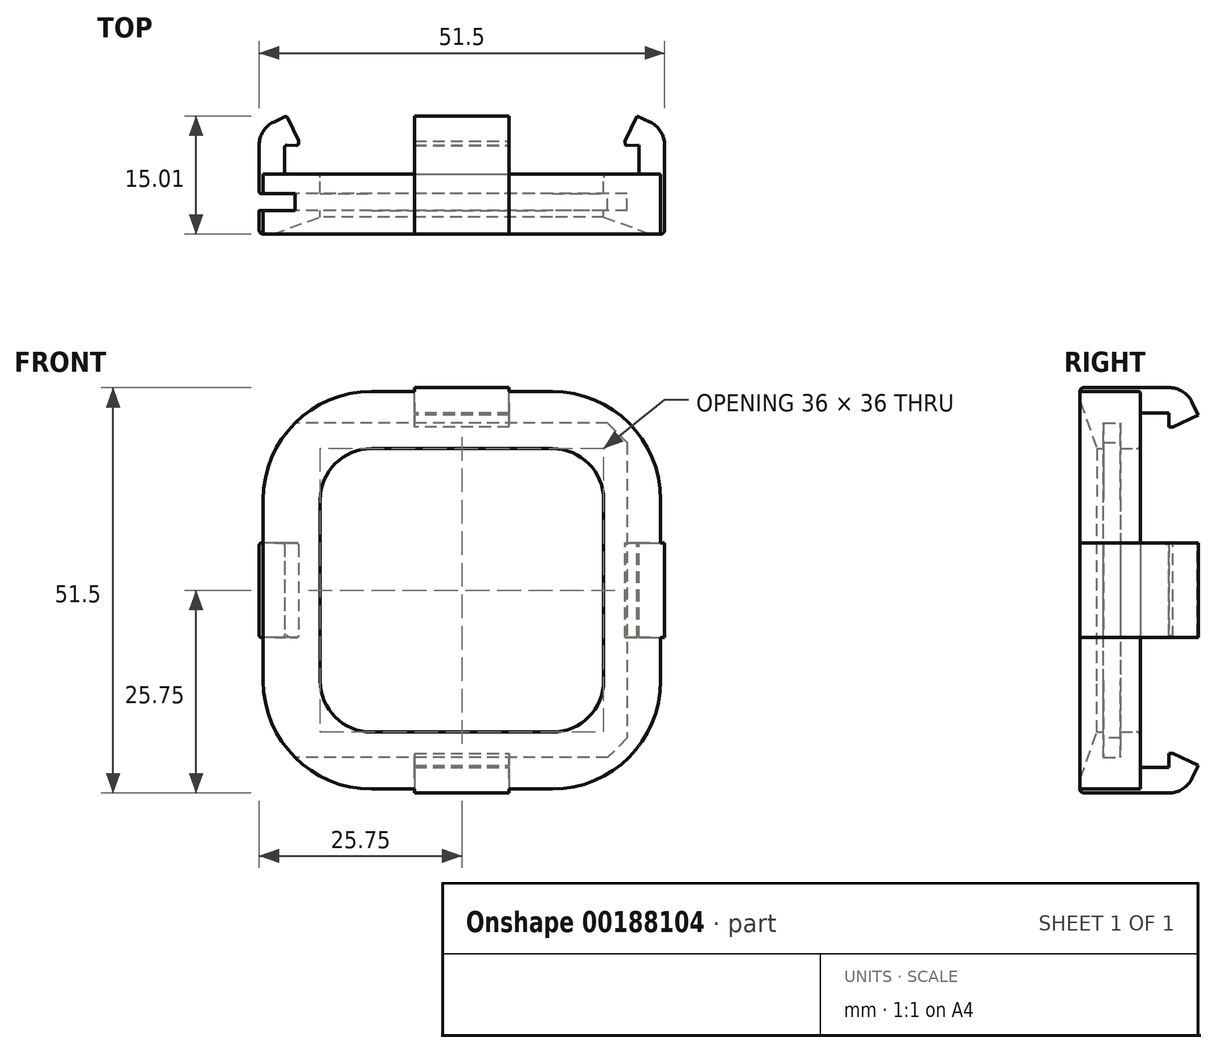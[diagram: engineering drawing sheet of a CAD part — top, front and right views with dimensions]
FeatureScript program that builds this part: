
annotation { "Feature Type Name" : "Feature", "Feature Type Description" : "" }
export const myFeature = defineFeature(function(context is Context, id is Id, definition is map)
    precondition{}
    {
        {
            var Q0;
            Q0=qCreatedBy(makeId("Front.planeOp"),FACE);
            var sketch = newSketch(context, id + "F0", { "sketchPlane" : qUnion([Q0])});
            skLineSegment(sketch, "E0.bottom", {"start": v(-11.5, 18) * mm, "end": v(11.5, 18) * mm});
            skLineSegment(sketch, "E0.top", {"start": v(-11.5, -18) * mm, "end": v(11.5, -18) * mm});
            skLineSegment(sketch, "E0.left", {"start": v(-18, 11.5) * mm, "end": v(-18, -11.5) * mm});
            skLineSegment(sketch, "E0.right", {"start": v(18, 11.5) * mm, "end": v(18, -11.5) * mm});
            skLineSegment(sketch, "E1", {"start": v(-11.5, 25.25) * mm, "end": v(11.5, 25.25) * mm});
            skLineSegment(sketch, "E2", {"start": v(25.25, 11.5) * mm, "end": v(25.25, -11.5) * mm});
            skLineSegment(sketch, "E3", {"start": v(11.5, -25.25) * mm, "end": v(-11.5, -25.25) * mm});
            skLineSegment(sketch, "E4", {"start": v(-25.25, -11.5) * mm, "end": v(-25.25, 11.5) * mm});
            skPoint(sketch, "E5.visualSharp", {"position": v(18, 18) * mm});
            skArc(sketch, "E5.filletArc", {"start": v(18, 11.5) * mm, "mid": v(16.1, 16.1) * mm, "end": v(11.5, 18) * mm});
            skPoint(sketch, "E6.visualSharp", {"position": v(-18, 18) * mm});
            skArc(sketch, "E6.filletArc", {"start": v(-11.5, 18) * mm, "mid": v(-16.1, 16.1) * mm, "end": v(-18, 11.5) * mm});
            skPoint(sketch, "E7.visualSharp", {"position": v(-18, -18) * mm});
            skArc(sketch, "E7.filletArc", {"start": v(-18, -11.5) * mm, "mid": v(-16.1, -16.1) * mm, "end": v(-11.5, -18) * mm});
            skPoint(sketch, "E8.visualSharp", {"position": v(18, -18) * mm});
            skArc(sketch, "E8.filletArc", {"start": v(11.5, -18) * mm, "mid": v(16.1, -16.1) * mm, "end": v(18, -11.5) * mm});
            skArc(sketch, "E9", {"start": v(-11.5, 25.25) * mm, "mid": v(-21.22, 21.22) * mm, "end": v(-25.25, 11.5) * mm});
            skArc(sketch, "E10", {"start": v(-25.25, -11.5) * mm, "mid": v(-21.22, -21.22) * mm, "end": v(-11.5, -25.25) * mm});
            skArc(sketch, "E11", {"start": v(11.5, -25.25) * mm, "mid": v(21.22, -21.22) * mm, "end": v(25.25, -11.5) * mm});
            skArc(sketch, "E12", {"start": v(25.25, 11.5) * mm, "mid": v(21.22, 21.22) * mm, "end": v(11.5, 25.25) * mm});
            skPoint(sketch, "E13.orphan", {"position": v(-25.25, 25.25) * mm});
            skPoint(sketch, "E14.orphan", {"position": v(-25.25, -25.25) * mm});
            skPoint(sketch, "E15.orphan", {"position": v(25.25, 25.25) * mm});
            skSolve(sketch);
        }
        {
            var Q0;
            Q0=makeQuery(id+"F0.imprint","IMPRINT",FACE,{"disambiguationData":[TD([[makeQuery(id+"F0.imprint","IMPRINT",EDGE,{"derivedFrom":sQuery(id+"F0.wireOp",EDGE,"E0.bottom")}),1.0]])]});
            extrude(context, id + "F1", {"entities" : qUnion([Q0]), "depth" : 7.65 * mm});
        }
        {
            var Q0;
            Q0=qCreatedBy(makeId("Right.planeOp"),FACE);
            var sketch = newSketch(context, id + "F2", { "sketchPlane" : qUnion([Q0])});
            skLineSegment(sketch, "E16", {"start": v(-2.5, 21.25) * mm, "end": v(-2.5, -21.25) * mm});
            skLineSegment(sketch, "E17", {"start": v(-2.5, -21.25) * mm, "end": v(-4.65, -21.25) * mm});
            skLineSegment(sketch, "E18", {"start": v(-4.65, -21.25) * mm, "end": v(-4.65, 21.25) * mm});
            skLineSegment(sketch, "E19", {"start": v(-4.65, 21.25) * mm, "end": v(-2.5, 21.25) * mm});
            skSolve(sketch);
        }
        {
            var Q0;
            Q0=makeQuery(id+"F2.imprint","IMPRINT",FACE,{"disambiguationData":[TD([[makeQuery(id+"F2.imprint","IMPRINT",EDGE,{"derivedFrom":sQuery(id+"F2.wireOp",EDGE,"E16")}),-1.0]])]});
            extrude(context, id + "F3", {"entities" : qUnion([Q0]), "operationType" : NewBodyOperationType.REMOVE, "depth" : 21 * mm, "hasSecondDirection" : true, "secondDirectionBound" : SecondDirectionBoundingType.THROUGH_ALL, "secondDirectionOppositeDirection" : true, "secondDirectionDepth" : 25 * mm});
        }
        {
            var Q0;
            Q0=makeQuery(id+"F3.boolean.opBoolean","COPY",EDGE,{"derivedFrom":makeQuery(id+"F3.opExtrude","CAP_EDGE",EDGE,{"disambiguationData":[OSD([sQuery(id+"F2.wireOp",EDGE,"E19")])],"isStart":false})});
            var Q1;
            Q1=makeQuery(id+"F3.boolean.opBoolean","COPY",EDGE,{"derivedFrom":makeQuery(id+"F3.opExtrude","CAP_EDGE",EDGE,{"disambiguationData":[OSD([sQuery(id+"F2.wireOp",EDGE,"E17")])],"isStart":false})});
            chamfer(context, id + "F4", {"entities" : qUnion([Q0, Q1]), "width" : 2.5 * mm, "tangentPropagation" : true});
        }
        {
            var Q0;
            Q0=makeQuery(id+"F1.opExtrude","CAP_EDGE",EDGE,{"disambiguationData":[OSD([sQuery(id+"F0.wireOp",EDGE,"E0.top")])],"isStart":false});
            chamfer(context, id + "F5", {"entities" : qUnion([Q0]), "chamferType" : ChamferType.TWO_OFFSETS, "width1" : 2.15 * mm, "oppositeDirection" : false, "width2" : 6 * mm, "tangentPropagation" : true});
        }
        {
            var Q0;
            Q0=qCreatedBy(makeId("Right.planeOp"),FACE);
            var sketch = newSketch(context, id + "F6", { "sketchPlane" : qUnion([Q0])});
            skLineSegment(sketch, "E20", {"start": v(0, 25.25) * mm, "end": v(-7.65, 25.25) * mm});
            skLineSegment(sketch, "E21", {"start": v(-7.15, 25.75) * mm, "end": v(3.65, 25.75) * mm});
            skLineSegment(sketch, "E22", {"start": v(0, 22.5) * mm, "end": v(3.65, 22.5) * mm});
            skArc(sketch, "E23", {"start": v(-7.65, 25.25) * mm, "mid": v(-7.5, 25.6) * mm, "end": v(-7.15, 25.75) * mm});
            skArc(sketch, "E24", {"start": v(3.65, 25.75) * mm, "mid": v(5.4, 25.24) * mm, "end": v(6.6, 23.88) * mm});
            skLineSegment(sketch, "E25", {"start": v(3.65, 22.5) * mm, "end": v(3.62, 20.75) * mm});
            skLineSegment(sketch, "E26", {"start": v(6.6, 23.88) * mm, "end": v(7.36, 22.25) * mm});
            skLineSegment(sketch, "E27", {"start": v(0, 22.5) * mm, "end": v(0, 25.25) * mm});
            skLineSegment(sketch, "E28", {"start": v(4.15, 20.74) * mm, "end": v(7.36, 22.25) * mm});
            skLineSegment(sketch, "E29", {"start": v(3.62, 20.75) * mm, "end": v(4.15, 20.74) * mm});
            skSolve(sketch);
        }
        {
            var Q0;
            Q0=makeQuery(id+"F6.imprint","IMPRINT",FACE,{"disambiguationData":[TD([[makeQuery(id+"F6.imprint","IMPRINT",EDGE,{"derivedFrom":sQuery(id+"F6.wireOp",EDGE,"E20")}),-1.0]])]});
            extrude(context, id + "F7", {"entities" : qUnion([Q0]), "endBound" : BoundingType.SYMMETRIC, "depth" : 12 * mm});
        }
        {
            var Q0;
            Q0=qCreatedBy(makeId("Right.planeOp"),FACE);
            var sketch = newSketch(context, id + "F8", { "sketchPlane" : qUnion([Q0])});
            skLineSegment(sketch, "E30", {"start": v(44.47, 0) * mm, "end": v(-52.9, 0) * mm, "construction": true});
            skSolve(sketch);
        }
        {
            var Q0;
            Q0=makeQuery(id+"F7.opExtrude","SWEPT_BODY",BODY,{"disambiguationData":[OSD([sQuery(id+"F6.wireOp",EDGE,"E20"),sQuery(id+"F6.wireOp",EDGE,"E21"),sQuery(id+"F6.wireOp",EDGE,"E22"),sQuery(id+"F6.wireOp",EDGE,"E23"),sQuery(id+"F6.wireOp",EDGE,"E24"),sQuery(id+"F6.wireOp",EDGE,"E25"),sQuery(id+"F6.wireOp",EDGE,"E26"),sQuery(id+"F6.wireOp",EDGE,"jlcA28JM-81w5-koXz-N9Zr-FnXAcRdSVXKj"),sQuery(id+"F6.wireOp",EDGE,"E27")])]});
            var Q1;
            Q1=sQuery(id+"F8.wireOp",EDGE,"E30");
            circularPattern(context, id + "F9", {"entities" : qUnion([Q0]), "axis" : qUnion([Q1]), "angle" : 90 * degree, "instanceCount" : 4, "oppositeDirection" : true});
        }
        {
            var Q0;
            Q0 = qSketchRegion(id + "F2", true);
            extrude(context, id + "F10", {"entities" : qUnion([Q0]), "operationType" : NewBodyOperationType.REMOVE, "endBound" : BoundingType.THROUGH_ALL, "oppositeDirection" : true, "depth" : 25 * mm});
        }
        {
            var Q0;
            Q0=makeQuery(id+"F9.opPattern","COPY",BODY,{"derivedFrom":makeQuery(id+"F7.opExtrude","SWEPT_BODY",BODY,{"disambiguationData":[OSD([sQuery(id+"F6.wireOp",EDGE,"E20"),sQuery(id+"F6.wireOp",EDGE,"E21"),sQuery(id+"F6.wireOp",EDGE,"E22"),sQuery(id+"F6.wireOp",EDGE,"E23"),sQuery(id+"F6.wireOp",EDGE,"E24"),sQuery(id+"F6.wireOp",EDGE,"E25"),sQuery(id+"F6.wireOp",EDGE,"E26"),sQuery(id+"F6.wireOp",EDGE,"E27"),sQuery(id+"F6.wireOp",EDGE,"E28"),sQuery(id+"F6.wireOp",EDGE,"E29")])]}),"instanceName":"2"});
            var Q1;
            Q1=makeQuery(id+"F9.opPattern","COPY",BODY,{"derivedFrom":makeQuery(id+"F7.opExtrude","SWEPT_BODY",BODY,{"disambiguationData":[OSD([sQuery(id+"F6.wireOp",EDGE,"E20"),sQuery(id+"F6.wireOp",EDGE,"E21"),sQuery(id+"F6.wireOp",EDGE,"E22"),sQuery(id+"F6.wireOp",EDGE,"E23"),sQuery(id+"F6.wireOp",EDGE,"E24"),sQuery(id+"F6.wireOp",EDGE,"E25"),sQuery(id+"F6.wireOp",EDGE,"E26"),sQuery(id+"F6.wireOp",EDGE,"E27"),sQuery(id+"F6.wireOp",EDGE,"E28"),sQuery(id+"F6.wireOp",EDGE,"E29")])]}),"instanceName":"1"});
            var Q2;
            Q2=makeQuery(id+"F1.opExtrude","SWEPT_BODY",BODY,{"disambiguationData":[OSD([sQuery(id+"F0.wireOp",EDGE,"E0.bottom"),sQuery(id+"F0.wireOp",EDGE,"E0.top"),sQuery(id+"F0.wireOp",EDGE,"E0.left"),sQuery(id+"F0.wireOp",EDGE,"E0.right"),sQuery(id+"F0.wireOp",EDGE,"E1"),sQuery(id+"F0.wireOp",EDGE,"E2"),sQuery(id+"F0.wireOp",EDGE,"E3"),sQuery(id+"F0.wireOp",EDGE,"E4"),sQuery(id+"F0.wireOp",EDGE,"E5.filletArc"),sQuery(id+"F0.wireOp",EDGE,"E6.filletArc"),sQuery(id+"F0.wireOp",EDGE,"E7.filletArc"),sQuery(id+"F0.wireOp",EDGE,"E8.filletArc"),sQuery(id+"F0.wireOp",EDGE,"E9"),sQuery(id+"F0.wireOp",EDGE,"E10"),sQuery(id+"F0.wireOp",EDGE,"E11"),sQuery(id+"F0.wireOp",EDGE,"E12")])]});
            var Q3;
            Q3=makeQuery(id+"F7.opExtrude","SWEPT_BODY",BODY,{"disambiguationData":[OSD([sQuery(id+"F6.wireOp",EDGE,"E20"),sQuery(id+"F6.wireOp",EDGE,"E21"),sQuery(id+"F6.wireOp",EDGE,"E22"),sQuery(id+"F6.wireOp",EDGE,"E23"),sQuery(id+"F6.wireOp",EDGE,"E24"),sQuery(id+"F6.wireOp",EDGE,"E25"),sQuery(id+"F6.wireOp",EDGE,"E26"),sQuery(id+"F6.wireOp",EDGE,"E27"),sQuery(id+"F6.wireOp",EDGE,"E28"),sQuery(id+"F6.wireOp",EDGE,"E29")])]});
            booleanBodies(context, id + "F11", {"operationType" : BooleanOperationType.UNION, "tools" : qUnion([Q0, Q1, Q2, Q3])});
        }
        {
            var Q0;
            Q0=makeQuery(id+"F7.opExtrude","CAP_EDGE",EDGE,{"disambiguationData":[OSD([sQuery(id+"F6.wireOp",EDGE,"E20")])],"isStart":true});
            var Q1;
            Q1=makeQuery(id+"F7.opExtrude","CAP_EDGE",EDGE,{"disambiguationData":[OSD([sQuery(id+"F6.wireOp",EDGE,"E27")])],"isStart":true});
            var Q2;
            {var subQ1=sQuery(id+"F0.wireOp",EDGE,"E9");var subQ2=sQuery(id+"F0.wireOp",EDGE,"E1");Q2=makeQuery(id+"F11.opBoolean","SPLIT",EDGE,{"disambiguationData":[TD([makeQuery(id+"F1.opExtrude","SWEPT_FACE",FACE,{"disambiguationData":[OSD([subQ1])]})])],"derivedFrom":makeQuery(id+"F1.opExtrude","CAP_EDGE",EDGE,{"disambiguationData":[OSD([subQ2])],"isStart":false})});}
            var Q3;
            Q3=makeQuery(id+"F7.opExtrude","CAP_EDGE",EDGE,{"disambiguationData":[OSD([sQuery(id+"F6.wireOp",EDGE,"E21")])],"isStart":true});
            var Q4;
            Q4=makeQuery(id+"F7.opExtrude","SWEPT_EDGE",EDGE,{"disambiguationData":[OSD([sQuery(id+"F6.wireOp",EDGE,"E26"),sQuery(id+"F6.wireOp",EDGE,"E28")])]});
            var Q5;
            Q5=makeQuery(id+"F7.opExtrude","CAP_EDGE",EDGE,{"disambiguationData":[OSD([sQuery(id+"F6.wireOp",EDGE,"E26")])],"isStart":false});
            var Q6;
            Q6=makeQuery(id+"F7.opExtrude","CAP_EDGE",EDGE,{"disambiguationData":[OSD([sQuery(id+"F6.wireOp",EDGE,"E20")])],"isStart":false});
            var Q7;
            Q7=makeQuery(id+"F7.opExtrude","CAP_EDGE",EDGE,{"disambiguationData":[OSD([sQuery(id+"F6.wireOp",EDGE,"E21")])],"isStart":false});
            var Q8;
            Q8=makeQuery(id+"F7.opExtrude","CAP_EDGE",EDGE,{"disambiguationData":[OSD([sQuery(id+"F6.wireOp",EDGE,"E24")])],"isStart":false});
            var Q9;
            Q9=makeQuery(id+"F7.opExtrude","CAP_EDGE",EDGE,{"disambiguationData":[OSD([sQuery(id+"F6.wireOp",EDGE,"E23")])],"isStart":false});
            var Q10;
            {var subQ1=sQuery(id+"F0.wireOp",EDGE,"E1");var subQ2=sQuery(id+"F0.wireOp",EDGE,"E12");Q10=makeQuery(id+"F11.opBoolean","SPLIT",EDGE,{"disambiguationData":[TD([makeQuery(id+"F1.opExtrude","SWEPT_FACE",FACE,{"disambiguationData":[OSD([subQ2])]})])],"derivedFrom":makeQuery(id+"F1.opExtrude","CAP_EDGE",EDGE,{"disambiguationData":[OSD([subQ1])],"isStart":false})});}
            var Q11;
            Q11=makeQuery(id+"F7.opExtrude","CAP_EDGE",EDGE,{"disambiguationData":[OSD([sQuery(id+"F6.wireOp",EDGE,"E27")])],"isStart":false});
            var Q12;
            Q12=makeQuery(id+"F7.opExtrude","SWEPT_EDGE",EDGE,{"disambiguationData":[OSD([sQuery(id+"F6.wireOp",EDGE,"E22"),sQuery(id+"F6.wireOp",EDGE,"E25")])]});
            var Q13;
            Q13=makeQuery(id+"F7.opExtrude","CAP_EDGE",EDGE,{"disambiguationData":[OSD([sQuery(id+"F6.wireOp",EDGE,"E25")])],"isStart":true});
            var Q14;
            Q14=makeQuery(id+"F7.opExtrude","CAP_EDGE",EDGE,{"disambiguationData":[OSD([sQuery(id+"F6.wireOp",EDGE,"E29")])],"isStart":true});
            var Q15;
            Q15=makeQuery(id+"F7.opExtrude","CAP_EDGE",EDGE,{"disambiguationData":[OSD([sQuery(id+"F6.wireOp",EDGE,"E28")])],"isStart":true});
            var Q16;
            Q16=makeQuery(id+"F7.opExtrude","SWEPT_EDGE",EDGE,{"disambiguationData":[OSD([sQuery(id+"F6.wireOp",EDGE,"E25"),sQuery(id+"F6.wireOp",EDGE,"E29")])]});
            var Q17;
            Q17=makeQuery(id+"F7.opExtrude","SWEPT_EDGE",EDGE,{"disambiguationData":[OSD([sQuery(id+"F6.wireOp",EDGE,"E28"),sQuery(id+"F6.wireOp",EDGE,"E29")])]});
            var Q18;
            Q18=makeQuery(id+"F7.opExtrude","CAP_EDGE",EDGE,{"disambiguationData":[OSD([sQuery(id+"F6.wireOp",EDGE,"E22")])],"isStart":false});
            var Q19;
            Q19=makeQuery(id+"F7.opExtrude","CAP_EDGE",EDGE,{"disambiguationData":[OSD([sQuery(id+"F6.wireOp",EDGE,"E28")])],"isStart":false});
            var Q20;
            Q20=makeQuery(id+"F7.opExtrude","CAP_EDGE",EDGE,{"disambiguationData":[OSD([sQuery(id+"F6.wireOp",EDGE,"E29")])],"isStart":false});
            var Q21;
            Q21=makeQuery(id+"F3.boolean.opBoolean","INTERSECT",EDGE,{"derivedFrom":[makeQuery(id+"F1.opExtrude","SWEPT_FACE",FACE,{"disambiguationData":[OSD([sQuery(id+"F0.wireOp",EDGE,"E4")])]}),makeQuery(id+"F3.opExtrude","SWEPT_FACE",FACE,{"disambiguationData":[OSD([sQuery(id+"F2.wireOp",EDGE,"E16")])]})]});
            var Q22;
            Q22=makeQuery(id+"F10.boolean.opBoolean","INTERSECT",EDGE,{"derivedFrom":[makeQuery(id+"F9.opPattern","COPY",FACE,{"derivedFrom":makeQuery(id+"F7.opExtrude","CAP_FACE",FACE,{"disambiguationData":[OSD([sQuery(id+"F6.wireOp",EDGE,"E20"),sQuery(id+"F6.wireOp",EDGE,"E21"),sQuery(id+"F6.wireOp",EDGE,"E22"),sQuery(id+"F6.wireOp",EDGE,"E23"),sQuery(id+"F6.wireOp",EDGE,"E24"),sQuery(id+"F6.wireOp",EDGE,"E25"),sQuery(id+"F6.wireOp",EDGE,"E26"),sQuery(id+"F6.wireOp",EDGE,"E27"),sQuery(id+"F6.wireOp",EDGE,"E28"),sQuery(id+"F6.wireOp",EDGE,"E29")])],"isStart":true}),"instanceName":"3"}),makeQuery(id+"F10.opExtrude","SWEPT_FACE",FACE,{"disambiguationData":[OSD([sQuery(id+"F2.wireOp",EDGE,"E16")])]})]});
            var Q23;
            {var subQ0=sQuery(id+"F0.wireOp",EDGE,"E9");var subQ1=sQuery(id+"F0.wireOp",EDGE,"E1");Q23=makeQuery(id+"F11.opBoolean","SPLIT",EDGE,{"disambiguationData":[TD([makeQuery(id+"F1.opExtrude","SWEPT_FACE",FACE,{"disambiguationData":[OSD([subQ0])]})])],"derivedFrom":makeQuery(id+"F1.opExtrude","CAP_EDGE",EDGE,{"disambiguationData":[OSD([subQ1])],"isStart":true})});}
            var Q24;
            Q24=makeQuery(id+"F9.opPattern","COPY",EDGE,{"derivedFrom":makeQuery(id+"F7.opExtrude","CAP_EDGE",EDGE,{"disambiguationData":[OSD([sQuery(id+"F6.wireOp",EDGE,"E20")])],"isStart":false}),"instanceName":"2"});
            var Q25;
            Q25=makeQuery(id+"F9.opPattern","COPY",EDGE,{"derivedFrom":makeQuery(id+"F7.opExtrude","CAP_EDGE",EDGE,{"disambiguationData":[OSD([sQuery(id+"F6.wireOp",EDGE,"E27")])],"isStart":false}),"instanceName":"2"});
            var Q26;
            Q26=makeQuery(id+"F9.opPattern","COPY",EDGE,{"derivedFrom":makeQuery(id+"F7.opExtrude","CAP_EDGE",EDGE,{"disambiguationData":[OSD([sQuery(id+"F6.wireOp",EDGE,"E23")])],"isStart":false}),"instanceName":"2"});
            var Q27;
            {var subQ1=sQuery(id+"F0.wireOp",EDGE,"E3");var subQ2=sQuery(id+"F0.wireOp",EDGE,"E10");Q27=makeQuery(id+"F11.opBoolean","SPLIT",EDGE,{"disambiguationData":[TD([makeQuery(id+"F1.opExtrude","SWEPT_FACE",FACE,{"disambiguationData":[OSD([subQ2])]})])],"derivedFrom":makeQuery(id+"F1.opExtrude","CAP_EDGE",EDGE,{"disambiguationData":[OSD([subQ1])],"isStart":false})});}
            var Q28;
            Q28=makeQuery(id+"F9.opPattern","COPY",EDGE,{"derivedFrom":makeQuery(id+"F7.opExtrude","CAP_EDGE",EDGE,{"disambiguationData":[OSD([sQuery(id+"F6.wireOp",EDGE,"E22")])],"isStart":false}),"instanceName":"2"});
            var Q29;
            Q29=makeQuery(id+"F9.opPattern","COPY",EDGE,{"derivedFrom":makeQuery(id+"F7.opExtrude","CAP_EDGE",EDGE,{"disambiguationData":[OSD([sQuery(id+"F6.wireOp",EDGE,"E25")])],"isStart":false}),"instanceName":"2"});
            var Q30;
            Q30=makeQuery(id+"F9.opPattern","COPY",EDGE,{"derivedFrom":makeQuery(id+"F7.opExtrude","CAP_EDGE",EDGE,{"disambiguationData":[OSD([sQuery(id+"F6.wireOp",EDGE,"E29")])],"isStart":false}),"instanceName":"2"});
            var Q31;
            Q31=makeQuery(id+"F9.opPattern","COPY",EDGE,{"derivedFrom":makeQuery(id+"F7.opExtrude","CAP_EDGE",EDGE,{"disambiguationData":[OSD([sQuery(id+"F6.wireOp",EDGE,"E28")])],"isStart":false}),"instanceName":"2"});
            var Q32;
            Q32=makeQuery(id+"F9.opPattern","COPY",EDGE,{"derivedFrom":makeQuery(id+"F7.opExtrude","SWEPT_EDGE",EDGE,{"disambiguationData":[OSD([sQuery(id+"F6.wireOp",EDGE,"E26"),sQuery(id+"F6.wireOp",EDGE,"E28")])]}),"instanceName":"2"});
            var Q33;
            Q33=makeQuery(id+"F9.opPattern","COPY",EDGE,{"derivedFrom":makeQuery(id+"F7.opExtrude","SWEPT_EDGE",EDGE,{"disambiguationData":[OSD([sQuery(id+"F6.wireOp",EDGE,"E28"),sQuery(id+"F6.wireOp",EDGE,"E29")])]}),"instanceName":"2"});
            var Q34;
            Q34=makeQuery(id+"F9.opPattern","COPY",EDGE,{"derivedFrom":makeQuery(id+"F7.opExtrude","SWEPT_EDGE",EDGE,{"disambiguationData":[OSD([sQuery(id+"F6.wireOp",EDGE,"E22"),sQuery(id+"F6.wireOp",EDGE,"E25")])]}),"instanceName":"2"});
            var Q35;
            Q35=makeQuery(id+"F9.opPattern","COPY",EDGE,{"derivedFrom":makeQuery(id+"F7.opExtrude","SWEPT_EDGE",EDGE,{"disambiguationData":[OSD([sQuery(id+"F6.wireOp",EDGE,"E25"),sQuery(id+"F6.wireOp",EDGE,"E29")])]}),"instanceName":"2"});
            var Q36;
            Q36=makeQuery(id+"F9.opPattern","COPY",EDGE,{"derivedFrom":makeQuery(id+"F7.opExtrude","CAP_EDGE",EDGE,{"disambiguationData":[OSD([sQuery(id+"F6.wireOp",EDGE,"E27")])],"isStart":true}),"instanceName":"2"});
            var Q37;
            Q37=makeQuery(id+"F9.opPattern","COPY",EDGE,{"derivedFrom":makeQuery(id+"F7.opExtrude","CAP_EDGE",EDGE,{"disambiguationData":[OSD([sQuery(id+"F6.wireOp",EDGE,"E22")])],"isStart":true}),"instanceName":"2"});
            var Q38;
            Q38=makeQuery(id+"F9.opPattern","COPY",EDGE,{"derivedFrom":makeQuery(id+"F7.opExtrude","CAP_EDGE",EDGE,{"disambiguationData":[OSD([sQuery(id+"F6.wireOp",EDGE,"E29")])],"isStart":true}),"instanceName":"2"});
            var Q39;
            Q39=makeQuery(id+"F9.opPattern","COPY",EDGE,{"derivedFrom":makeQuery(id+"F7.opExtrude","CAP_EDGE",EDGE,{"disambiguationData":[OSD([sQuery(id+"F6.wireOp",EDGE,"E28")])],"isStart":true}),"instanceName":"2"});
            var Q40;
            Q40=makeQuery(id+"F9.opPattern","COPY",EDGE,{"derivedFrom":makeQuery(id+"F7.opExtrude","CAP_EDGE",EDGE,{"disambiguationData":[OSD([sQuery(id+"F6.wireOp",EDGE,"E26")])],"isStart":true}),"instanceName":"2"});
            var Q41;
            Q41=makeQuery(id+"F9.opPattern","COPY",EDGE,{"derivedFrom":makeQuery(id+"F7.opExtrude","CAP_EDGE",EDGE,{"disambiguationData":[OSD([sQuery(id+"F6.wireOp",EDGE,"E20")])],"isStart":true}),"instanceName":"2"});
            var Q42;
            {var subQ1=sQuery(id+"F0.wireOp",EDGE,"E11");var subQ2=sQuery(id+"F0.wireOp",EDGE,"E3");Q42=makeQuery(id+"F11.opBoolean","SPLIT",EDGE,{"disambiguationData":[TD([makeQuery(id+"F1.opExtrude","SWEPT_FACE",FACE,{"disambiguationData":[OSD([subQ1])]})])],"derivedFrom":makeQuery(id+"F1.opExtrude","CAP_EDGE",EDGE,{"disambiguationData":[OSD([subQ2])],"isStart":false})});}
            var Q43;
            Q43=makeQuery(id+"F9.opPattern","COPY",EDGE,{"derivedFrom":makeQuery(id+"F7.opExtrude","CAP_EDGE",EDGE,{"disambiguationData":[OSD([sQuery(id+"F6.wireOp",EDGE,"E23")])],"isStart":false}),"instanceName":"1"});
            var Q44;
            Q44=makeQuery(id+"F9.opPattern","COPY",EDGE,{"derivedFrom":makeQuery(id+"F7.opExtrude","CAP_EDGE",EDGE,{"disambiguationData":[OSD([sQuery(id+"F6.wireOp",EDGE,"E20")])],"isStart":false}),"instanceName":"1"});
            var Q45;
            Q45=makeQuery(id+"F9.opPattern","COPY",EDGE,{"derivedFrom":makeQuery(id+"F7.opExtrude","CAP_EDGE",EDGE,{"disambiguationData":[OSD([sQuery(id+"F6.wireOp",EDGE,"E27")])],"isStart":false}),"instanceName":"1"});
            var Q46;
            {var subQ0=sQuery(id+"F0.wireOp",EDGE,"E11");var subQ1=sQuery(id+"F0.wireOp",EDGE,"E2");Q46=makeQuery(id+"F11.opBoolean","SPLIT",EDGE,{"disambiguationData":[TD([makeQuery(id+"F1.opExtrude","SWEPT_FACE",FACE,{"disambiguationData":[OSD([subQ0])]})])],"derivedFrom":makeQuery(id+"F1.opExtrude","CAP_EDGE",EDGE,{"disambiguationData":[OSD([subQ1])],"isStart":true})});}
            var Q47;
            Q47=makeQuery(id+"F9.opPattern","COPY",EDGE,{"derivedFrom":makeQuery(id+"F7.opExtrude","CAP_EDGE",EDGE,{"disambiguationData":[OSD([sQuery(id+"F6.wireOp",EDGE,"E22")])],"isStart":false}),"instanceName":"1"});
            var Q48;
            Q48=makeQuery(id+"F9.opPattern","COPY",EDGE,{"derivedFrom":makeQuery(id+"F7.opExtrude","SWEPT_EDGE",EDGE,{"disambiguationData":[OSD([sQuery(id+"F6.wireOp",EDGE,"E22"),sQuery(id+"F6.wireOp",EDGE,"E25")])]}),"instanceName":"1"});
            var Q49;
            Q49=makeQuery(id+"F9.opPattern","COPY",EDGE,{"derivedFrom":makeQuery(id+"F7.opExtrude","SWEPT_EDGE",EDGE,{"disambiguationData":[OSD([sQuery(id+"F6.wireOp",EDGE,"E25"),sQuery(id+"F6.wireOp",EDGE,"E29")])]}),"instanceName":"1"});
            var Q50;
            Q50=makeQuery(id+"F9.opPattern","COPY",EDGE,{"derivedFrom":makeQuery(id+"F7.opExtrude","CAP_EDGE",EDGE,{"disambiguationData":[OSD([sQuery(id+"F6.wireOp",EDGE,"E29")])],"isStart":false}),"instanceName":"1"});
            var Q51;
            Q51=makeQuery(id+"F9.opPattern","COPY",EDGE,{"derivedFrom":makeQuery(id+"F7.opExtrude","SWEPT_EDGE",EDGE,{"disambiguationData":[OSD([sQuery(id+"F6.wireOp",EDGE,"E28"),sQuery(id+"F6.wireOp",EDGE,"E29")])]}),"instanceName":"1"});
            var Q52;
            Q52=makeQuery(id+"F9.opPattern","COPY",EDGE,{"derivedFrom":makeQuery(id+"F7.opExtrude","CAP_EDGE",EDGE,{"disambiguationData":[OSD([sQuery(id+"F6.wireOp",EDGE,"E28")])],"isStart":false}),"instanceName":"1"});
            var Q53;
            Q53=makeQuery(id+"F9.opPattern","COPY",EDGE,{"derivedFrom":makeQuery(id+"F7.opExtrude","SWEPT_EDGE",EDGE,{"disambiguationData":[OSD([sQuery(id+"F6.wireOp",EDGE,"E26"),sQuery(id+"F6.wireOp",EDGE,"E28")])]}),"instanceName":"1"});
            var Q54;
            Q54=makeQuery(id+"F9.opPattern","COPY",EDGE,{"derivedFrom":makeQuery(id+"F7.opExtrude","CAP_EDGE",EDGE,{"disambiguationData":[OSD([sQuery(id+"F6.wireOp",EDGE,"E22")])],"isStart":true}),"instanceName":"1"});
            var Q55;
            Q55=makeQuery(id+"F9.opPattern","COPY",EDGE,{"derivedFrom":makeQuery(id+"F7.opExtrude","CAP_EDGE",EDGE,{"disambiguationData":[OSD([sQuery(id+"F6.wireOp",EDGE,"E29")])],"isStart":true}),"instanceName":"1"});
            var Q56;
            Q56=makeQuery(id+"F9.opPattern","COPY",EDGE,{"derivedFrom":makeQuery(id+"F7.opExtrude","CAP_EDGE",EDGE,{"disambiguationData":[OSD([sQuery(id+"F6.wireOp",EDGE,"E28")])],"isStart":true}),"instanceName":"1"});
            var Q57;
            Q57=makeQuery(id+"F9.opPattern","COPY",EDGE,{"derivedFrom":makeQuery(id+"F7.opExtrude","CAP_EDGE",EDGE,{"disambiguationData":[OSD([sQuery(id+"F6.wireOp",EDGE,"E26")])],"isStart":true}),"instanceName":"1"});
            var Q58;
            Q58=makeQuery(id+"F9.opPattern","COPY",EDGE,{"derivedFrom":makeQuery(id+"F7.opExtrude","CAP_EDGE",EDGE,{"disambiguationData":[OSD([sQuery(id+"F6.wireOp",EDGE,"E20")])],"isStart":true}),"instanceName":"1"});
            var Q59;
            {var subQ0=sQuery(id+"F6.wireOp",EDGE,"E24");var subQ1=sQuery(id+"F6.wireOp",EDGE,"E21");Q59=makeQuery(id+"F10.boolean.opBoolean","SPLIT",EDGE,{"disambiguationData":[TD([makeQuery(id+"F9.opPattern","COPY",FACE,{"derivedFrom":makeQuery(id+"F7.opExtrude","SWEPT_FACE",FACE,{"disambiguationData":[OSD([subQ0])]}),"instanceName":"3"})])],"derivedFrom":makeQuery(id+"F9.opPattern","COPY",EDGE,{"derivedFrom":makeQuery(id+"F7.opExtrude","CAP_EDGE",EDGE,{"disambiguationData":[OSD([subQ1])],"isStart":true}),"instanceName":"3"})});}
            var Q60;
            Q60=makeQuery(id+"F10.boolean.opBoolean","INTERSECT",EDGE,{"derivedFrom":[makeQuery(id+"F9.opPattern","COPY",FACE,{"derivedFrom":makeQuery(id+"F7.opExtrude","SWEPT_FACE",FACE,{"disambiguationData":[OSD([sQuery(id+"F6.wireOp",EDGE,"E21")])]}),"instanceName":"3"}),makeQuery(id+"F10.opExtrude","SWEPT_FACE",FACE,{"disambiguationData":[OSD([sQuery(id+"F2.wireOp",EDGE,"E16")])]})]});
            var Q61;
            Q61=makeQuery(id+"F10.boolean.opBoolean","INTERSECT",EDGE,{"derivedFrom":[makeQuery(id+"F9.opPattern","COPY",FACE,{"derivedFrom":makeQuery(id+"F7.opExtrude","CAP_FACE",FACE,{"disambiguationData":[OSD([sQuery(id+"F6.wireOp",EDGE,"E20"),sQuery(id+"F6.wireOp",EDGE,"E21"),sQuery(id+"F6.wireOp",EDGE,"E22"),sQuery(id+"F6.wireOp",EDGE,"E23"),sQuery(id+"F6.wireOp",EDGE,"E24"),sQuery(id+"F6.wireOp",EDGE,"E25"),sQuery(id+"F6.wireOp",EDGE,"E26"),sQuery(id+"F6.wireOp",EDGE,"E27"),sQuery(id+"F6.wireOp",EDGE,"E28"),sQuery(id+"F6.wireOp",EDGE,"E29")])],"isStart":false}),"instanceName":"3"}),makeQuery(id+"F10.opExtrude","SWEPT_FACE",FACE,{"disambiguationData":[OSD([sQuery(id+"F2.wireOp",EDGE,"E16")])]})]});
            var Q62;
            {var subQ0=sQuery(id+"F6.wireOp",EDGE,"E24");var subQ1=sQuery(id+"F6.wireOp",EDGE,"E21");Q62=makeQuery(id+"F10.boolean.opBoolean","SPLIT",EDGE,{"disambiguationData":[TD([makeQuery(id+"F9.opPattern","COPY",FACE,{"derivedFrom":makeQuery(id+"F7.opExtrude","SWEPT_FACE",FACE,{"disambiguationData":[OSD([subQ0])]}),"instanceName":"3"})])],"derivedFrom":makeQuery(id+"F9.opPattern","COPY",EDGE,{"derivedFrom":makeQuery(id+"F7.opExtrude","CAP_EDGE",EDGE,{"disambiguationData":[OSD([subQ1])],"isStart":false}),"instanceName":"3"})});}
            var Q63;
            Q63=makeQuery(id+"F9.opPattern","COPY",EDGE,{"derivedFrom":makeQuery(id+"F7.opExtrude","SWEPT_EDGE",EDGE,{"disambiguationData":[OSD([sQuery(id+"F6.wireOp",EDGE,"E26"),sQuery(id+"F6.wireOp",EDGE,"E28")])]}),"instanceName":"3"});
            var Q64;
            Q64=makeQuery(id+"F9.opPattern","COPY",EDGE,{"derivedFrom":makeQuery(id+"F7.opExtrude","CAP_EDGE",EDGE,{"disambiguationData":[OSD([sQuery(id+"F6.wireOp",EDGE,"E28")])],"isStart":false}),"instanceName":"3"});
            var Q65;
            Q65=makeQuery(id+"F9.opPattern","COPY",EDGE,{"derivedFrom":makeQuery(id+"F7.opExtrude","SWEPT_EDGE",EDGE,{"disambiguationData":[OSD([sQuery(id+"F6.wireOp",EDGE,"E28"),sQuery(id+"F6.wireOp",EDGE,"E29")])]}),"instanceName":"3"});
            var Q66;
            Q66=makeQuery(id+"F9.opPattern","COPY",EDGE,{"derivedFrom":makeQuery(id+"F7.opExtrude","CAP_EDGE",EDGE,{"disambiguationData":[OSD([sQuery(id+"F6.wireOp",EDGE,"E29")])],"isStart":false}),"instanceName":"3"});
            var Q67;
            Q67=makeQuery(id+"F9.opPattern","COPY",EDGE,{"derivedFrom":makeQuery(id+"F7.opExtrude","SWEPT_EDGE",EDGE,{"disambiguationData":[OSD([sQuery(id+"F6.wireOp",EDGE,"E25"),sQuery(id+"F6.wireOp",EDGE,"E29")])]}),"instanceName":"3"});
            var Q68;
            Q68=makeQuery(id+"F9.opPattern","COPY",EDGE,{"derivedFrom":makeQuery(id+"F7.opExtrude","CAP_EDGE",EDGE,{"disambiguationData":[OSD([sQuery(id+"F6.wireOp",EDGE,"E25")])],"isStart":false}),"instanceName":"3"});
            var Q69;
            Q69=makeQuery(id+"F9.opPattern","COPY",EDGE,{"derivedFrom":makeQuery(id+"F7.opExtrude","SWEPT_EDGE",EDGE,{"disambiguationData":[OSD([sQuery(id+"F6.wireOp",EDGE,"E22"),sQuery(id+"F6.wireOp",EDGE,"E25")])]}),"instanceName":"3"});
            var Q70;
            Q70=makeQuery(id+"F9.opPattern","COPY",EDGE,{"derivedFrom":makeQuery(id+"F7.opExtrude","CAP_EDGE",EDGE,{"disambiguationData":[OSD([sQuery(id+"F6.wireOp",EDGE,"E22")])],"isStart":true}),"instanceName":"3"});
            var Q71;
            Q71=makeQuery(id+"F9.opPattern","COPY",EDGE,{"derivedFrom":makeQuery(id+"F7.opExtrude","CAP_EDGE",EDGE,{"disambiguationData":[OSD([sQuery(id+"F6.wireOp",EDGE,"E29")])],"isStart":true}),"instanceName":"3"});
            var Q72;
            Q72=makeQuery(id+"F9.opPattern","COPY",EDGE,{"derivedFrom":makeQuery(id+"F7.opExtrude","CAP_EDGE",EDGE,{"disambiguationData":[OSD([sQuery(id+"F6.wireOp",EDGE,"E28")])],"isStart":true}),"instanceName":"3"});
            var Q73;
            {var subQ0=sQuery(id+"F6.wireOp",EDGE,"E23");var subQ1=sQuery(id+"F6.wireOp",EDGE,"E21");Q73=makeQuery(id+"F10.boolean.opBoolean","SPLIT",EDGE,{"disambiguationData":[TD([makeQuery(id+"F9.opPattern","COPY",FACE,{"derivedFrom":makeQuery(id+"F7.opExtrude","SWEPT_FACE",FACE,{"disambiguationData":[OSD([subQ0])]}),"instanceName":"3"})])],"derivedFrom":makeQuery(id+"F9.opPattern","COPY",EDGE,{"derivedFrom":makeQuery(id+"F7.opExtrude","CAP_EDGE",EDGE,{"disambiguationData":[OSD([subQ1])],"isStart":false}),"instanceName":"3"})});}
            var Q74;
            {var subQ0=sQuery(id+"F6.wireOp",EDGE,"E23");var subQ1=sQuery(id+"F6.wireOp",EDGE,"E21");Q74=makeQuery(id+"F10.boolean.opBoolean","SPLIT",EDGE,{"disambiguationData":[TD([makeQuery(id+"F9.opPattern","COPY",FACE,{"derivedFrom":makeQuery(id+"F7.opExtrude","SWEPT_FACE",FACE,{"disambiguationData":[OSD([subQ0])]}),"instanceName":"3"})])],"derivedFrom":makeQuery(id+"F9.opPattern","COPY",EDGE,{"derivedFrom":makeQuery(id+"F7.opExtrude","CAP_EDGE",EDGE,{"disambiguationData":[OSD([subQ1])],"isStart":true}),"instanceName":"3"})});}
            fillet(context, id + "F12", {"entities" : qUnion([Q0, Q1, Q2, Q3, Q4, Q5, Q6, Q7, Q8, Q9, Q10, Q11, Q12, Q13, Q14, Q15, Q16, Q17, Q18, Q19, Q20, Q21, Q22, Q23, Q24, Q25, Q26, Q27, Q28, Q29, Q30, Q31, Q32, Q33, Q34, Q35, Q36, Q37, Q38, Q39, Q40, Q41, Q42, Q43, Q44, Q45, Q46, Q47, Q48, Q49, Q50, Q51, Q52, Q53, Q54, Q55, Q56, Q57, Q58, Q59, Q60, Q61, Q62, Q63, Q64, Q65, Q66, Q67, Q68, Q69, Q70, Q71, Q72, Q73, Q74]), "radius" : .25 * mm, "tangentPropagation" : true, "allowEdgeOverflow" : false});
        }
        {
            var Q0;
            Q0=makeQuery(id+"F1.opExtrude","CAP_EDGE",EDGE,{"disambiguationData":[OSD([sQuery(id+"F0.wireOp",EDGE,"E12")])],"isStart":true});
            fillet(context, id + "F13", {"entities" : qUnion([Q0]), "radius" : .25 * mm, "tangentPropagation" : true, "allowEdgeOverflow" : false});
        }
        {
            var Q0;
            Q0=makeQuery(id+"F1.opExtrude","CAP_EDGE",EDGE,{"disambiguationData":[OSD([sQuery(id+"F0.wireOp",EDGE,"E0.top")])],"isStart":true});
            fillet(context, id + "F14", {"entities" : qUnion([Q0]), "radius" : .5 * mm, "tangentPropagation" : true, "allowEdgeOverflow" : false});
        }
        {
            var Q0;
            {var subQ0=sQuery(id+"F0.wireOp",EDGE,"E7.filletArc");Q0=makeQuery(id+"F5.opChamfer","BLEND_EDGE",EDGE,{"blendedFrom":[makeQuery(id+"F1.opExtrude","CAP_EDGE",EDGE,{"disambiguationData":[OSD([subQ0])],"isStart":false}),makeQuery(id+"F1.opExtrude","CAP_FACE",FACE,{"disambiguationData":[OSD([sQuery(id+"F0.wireOp",EDGE,"E0.bottom"),sQuery(id+"F0.wireOp",EDGE,"E0.top"),sQuery(id+"F0.wireOp",EDGE,"E0.left"),sQuery(id+"F0.wireOp",EDGE,"E0.right"),sQuery(id+"F0.wireOp",EDGE,"E1"),sQuery(id+"F0.wireOp",EDGE,"E2"),sQuery(id+"F0.wireOp",EDGE,"E3"),sQuery(id+"F0.wireOp",EDGE,"E4"),sQuery(id+"F0.wireOp",EDGE,"E5.filletArc"),sQuery(id+"F0.wireOp",EDGE,"E6.filletArc"),subQ0,sQuery(id+"F0.wireOp",EDGE,"E8.filletArc"),sQuery(id+"F0.wireOp",EDGE,"E9"),sQuery(id+"F0.wireOp",EDGE,"E10"),sQuery(id+"F0.wireOp",EDGE,"E11"),sQuery(id+"F0.wireOp",EDGE,"E12")])],"isStart":false})],"blendedInto":[makeQuery(id+"F1.opExtrude","CAP_FACE",FACE,{"disambiguationData":[OSD([sQuery(id+"F0.wireOp",EDGE,"E0.bottom"),sQuery(id+"F0.wireOp",EDGE,"E0.top"),sQuery(id+"F0.wireOp",EDGE,"E0.left"),sQuery(id+"F0.wireOp",EDGE,"E0.right"),sQuery(id+"F0.wireOp",EDGE,"E1"),sQuery(id+"F0.wireOp",EDGE,"E2"),sQuery(id+"F0.wireOp",EDGE,"E3"),sQuery(id+"F0.wireOp",EDGE,"E4"),sQuery(id+"F0.wireOp",EDGE,"E5.filletArc"),sQuery(id+"F0.wireOp",EDGE,"E6.filletArc"),subQ0,sQuery(id+"F0.wireOp",EDGE,"E8.filletArc"),sQuery(id+"F0.wireOp",EDGE,"E9"),sQuery(id+"F0.wireOp",EDGE,"E10"),sQuery(id+"F0.wireOp",EDGE,"E11"),sQuery(id+"F0.wireOp",EDGE,"E12")])],"isStart":false})]});}
            fillet(context, id + "F15", {"entities" : qUnion([Q0]), "radius" : .5 * mm, "tangentPropagation" : true, "allowEdgeOverflow" : false});
        }
    });
